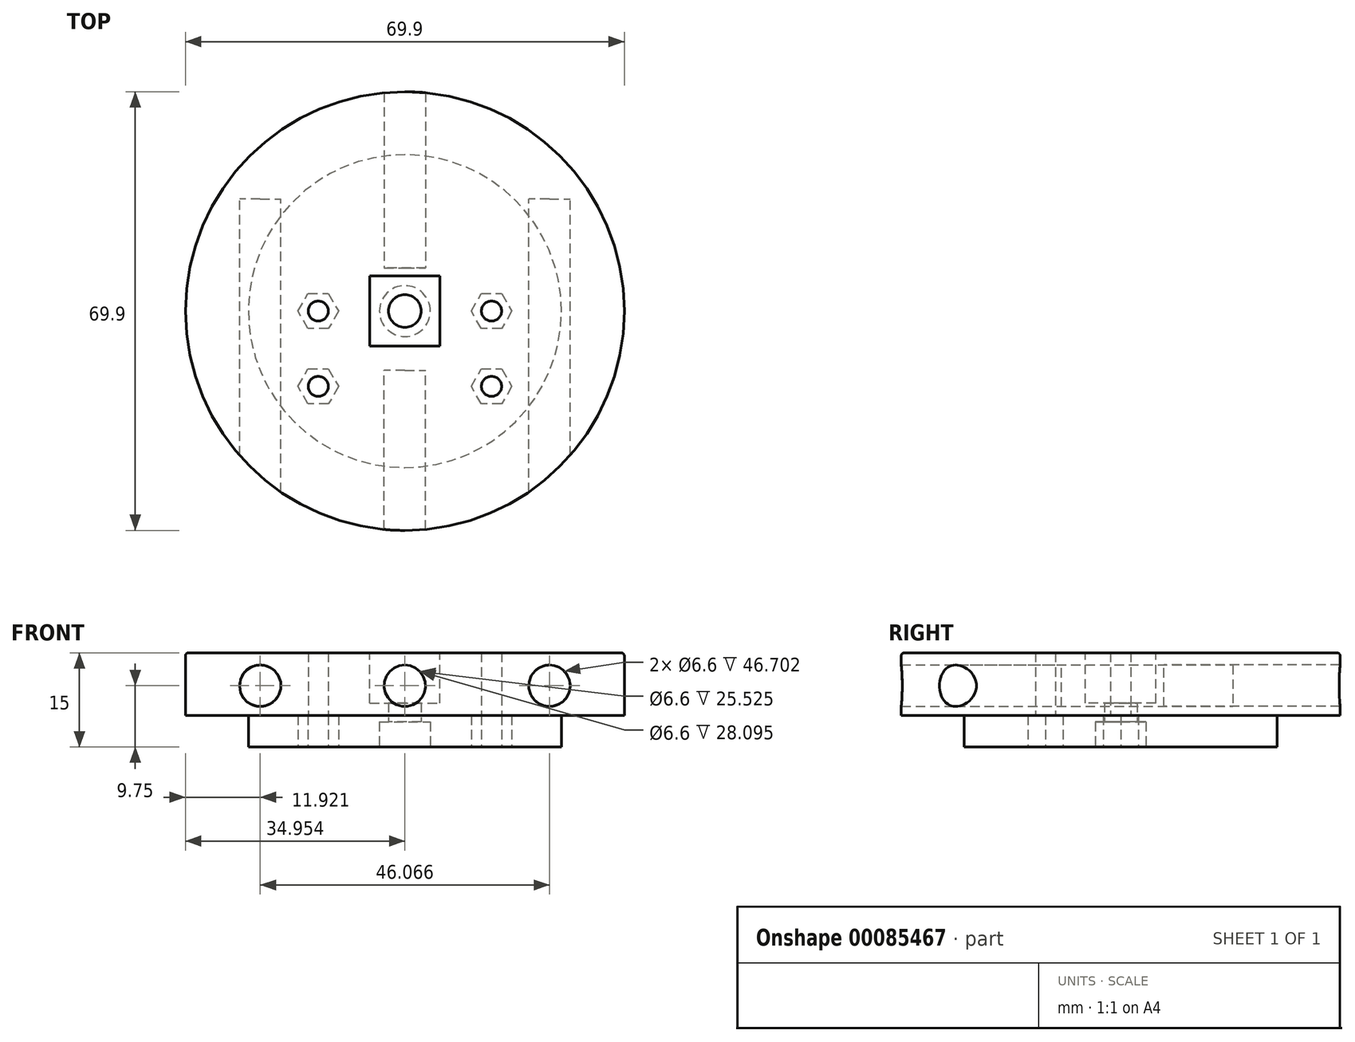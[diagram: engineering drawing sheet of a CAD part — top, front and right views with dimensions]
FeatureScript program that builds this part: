
annotation { "Feature Type Name" : "Feature", "Feature Type Description" : "" }
export const myFeature = defineFeature(function(context is Context, id is Id, definition is map)
    precondition{}
    {
        {
            var Q0;
            Q0=qCreatedBy(makeId("Top.planeOp"),FACE);
            var sketch = newSketch(context, id + "F0", { "sketchPlane" : qUnion([Q0])});
            skCircle(sketch, "E0", {"center": v(30.33, -8.57) * mm, "radius": 34.95 * mm});
            skLineSegment(sketch, "E1.bottom", {"start": v(35.93, -14.17) * mm, "end": v(24.73, -14.17) * mm});
            skLineSegment(sketch, "E1.top", {"start": v(35.93, -2.97) * mm, "end": v(24.73, -2.97) * mm});
            skLineSegment(sketch, "E1.left", {"start": v(35.93, -14.17) * mm, "end": v(35.93, -2.97) * mm});
            skLineSegment(sketch, "E1.right", {"start": v(24.73, -14.17) * mm, "end": v(24.73, -2.97) * mm});
            skPoint(sketch, "E2", {"position": v(24.73, -2.97) * mm});
            skLineSegment(sketch, "E3", {"start": v(30.33, -8.57) * mm, "end": v(5.62, -33.29) * mm, "construction": true});
            skLineSegment(sketch, "E4", {"start": v(30.33, -8.57) * mm, "end": v(55.05, 16.14) * mm, "construction": true});
            skCircle(sketch, "E5", {"center": v(30.33, -8.57) * mm, "radius": 24.93 * mm});
            skLineSegment(sketch, "E6", {"start": v(24.73, -14.17) * mm, "end": v(24.73, -43.07) * mm, "construction": true});
            skLineSegment(sketch, "E7", {"start": v(35.93, -14.17) * mm, "end": v(35.93, -43.07) * mm, "construction": true});
            skPoint(sketch, "E8", {"position": v(16.53, -20.57) * mm});
            skPoint(sketch, "E9", {"position": v(16.53, -8.57) * mm});
            skPoint(sketch, "E10", {"position": v(44.13, -8.57) * mm});
            skPoint(sketch, "E11", {"position": v(44.13, -20.57) * mm});
            skCircle(sketch, "E12.cCircle", {"center": v(16.53, -20.57) * mm, "radius": 3.23 * mm, "construction": true});
            skLineSegment(sketch, "E12.0", {"start": v(19.77, -20.57) * mm, "end": v(18.15, -23.37) * mm});
            skLineSegment(sketch, "E12.1", {"start": v(18.15, -23.37) * mm, "end": v(14.92, -23.37) * mm});
            skLineSegment(sketch, "E12.2", {"start": v(14.92, -23.37) * mm, "end": v(13.3, -20.57) * mm});
            skLineSegment(sketch, "E12.3", {"start": v(13.3, -20.57) * mm, "end": v(14.92, -17.77) * mm});
            skLineSegment(sketch, "E12.4", {"start": v(14.92, -17.77) * mm, "end": v(18.15, -17.77) * mm});
            skLineSegment(sketch, "E12.5", {"start": v(18.15, -17.77) * mm, "end": v(19.77, -20.57) * mm});
            skCircle(sketch, "E13.cCircle", {"center": v(16.53, -8.57) * mm, "radius": 3.23 * mm, "construction": true});
            skLineSegment(sketch, "E13.0", {"start": v(13.3, -8.57) * mm, "end": v(14.92, -5.77) * mm});
            skLineSegment(sketch, "E13.1", {"start": v(14.92, -5.77) * mm, "end": v(18.15, -5.77) * mm});
            skLineSegment(sketch, "E13.2", {"start": v(18.15, -5.77) * mm, "end": v(19.77, -8.57) * mm});
            skLineSegment(sketch, "E13.3", {"start": v(19.77, -8.57) * mm, "end": v(18.15, -11.37) * mm});
            skLineSegment(sketch, "E13.4", {"start": v(18.15, -11.37) * mm, "end": v(14.92, -11.37) * mm});
            skLineSegment(sketch, "E13.5", {"start": v(14.92, -11.37) * mm, "end": v(13.3, -8.57) * mm});
            skCircle(sketch, "E14.cCircle", {"center": v(44.13, -8.57) * mm, "radius": 3.23 * mm, "construction": true});
            skLineSegment(sketch, "E14.0", {"start": v(40.9, -8.57) * mm, "end": v(42.52, -5.77) * mm});
            skLineSegment(sketch, "E14.1", {"start": v(42.52, -5.77) * mm, "end": v(45.75, -5.77) * mm});
            skLineSegment(sketch, "E14.2", {"start": v(45.75, -5.77) * mm, "end": v(47.37, -8.57) * mm});
            skLineSegment(sketch, "E14.3", {"start": v(47.37, -8.57) * mm, "end": v(45.75, -11.37) * mm});
            skLineSegment(sketch, "E14.4", {"start": v(45.75, -11.37) * mm, "end": v(42.52, -11.37) * mm});
            skLineSegment(sketch, "E14.5", {"start": v(42.52, -11.37) * mm, "end": v(40.9, -8.57) * mm});
            skCircle(sketch, "E15.cCircle", {"center": v(44.13, -20.57) * mm, "radius": 3.23 * mm, "construction": true});
            skLineSegment(sketch, "E15.0", {"start": v(47.37, -20.57) * mm, "end": v(45.75, -23.37) * mm});
            skLineSegment(sketch, "E15.1", {"start": v(45.75, -23.37) * mm, "end": v(42.52, -23.37) * mm});
            skLineSegment(sketch, "E15.2", {"start": v(42.52, -23.37) * mm, "end": v(40.9, -20.57) * mm});
            skLineSegment(sketch, "E15.3", {"start": v(40.9, -20.57) * mm, "end": v(42.52, -17.77) * mm});
            skLineSegment(sketch, "E15.4", {"start": v(42.52, -17.77) * mm, "end": v(45.75, -17.77) * mm});
            skLineSegment(sketch, "E15.5", {"start": v(45.75, -17.77) * mm, "end": v(47.37, -20.57) * mm});
            skLineSegment(sketch, "E16", {"start": v(16.53, -8.57) * mm, "end": v(44.13, -8.57) * mm, "construction": true});
            skLineSegment(sketch, "E17", {"start": v(16.53, -20.57) * mm, "end": v(44.13, -20.57) * mm, "construction": true});
            skLineSegment(sketch, "E18", {"start": v(16.53, -8.57) * mm, "end": v(16.53, -20.57) * mm, "construction": true});
            skLineSegment(sketch, "E19", {"start": v(44.13, -20.57) * mm, "end": v(44.13, -8.57) * mm, "construction": true});
            skLineSegment(sketch, "E20", {"start": v(30.33, -20.57) * mm, "end": v(30.33, -8.57) * mm, "construction": true});
            skLineSegment(sketch, "E21", {"start": v(30.33, -8.57) * mm, "end": v(24.73, -8.57) * mm, "construction": true});
            skLineSegment(sketch, "E22", {"start": v(24.73, -8.57) * mm, "end": v(24.73, -20.57) * mm, "construction": true});
            skLineSegment(sketch, "E23", {"start": v(30.33, -8.57) * mm, "end": v(35.93, -8.57) * mm, "construction": true});
            skLineSegment(sketch, "E24", {"start": v(35.93, -8.57) * mm, "end": v(35.93, -20.57) * mm, "construction": true});
            skLineSegment(sketch, "E25", {"start": v(24.73, -8.57) * mm, "end": v(24.73, -14.17) * mm, "construction": true});
            skLineSegment(sketch, "E26", {"start": v(24.73, -8.57) * mm, "end": v(35.93, -8.57) * mm, "construction": true});
            skCircle(sketch, "E27", {"center": v(16.53, -8.57) * mm, "radius": 1.6 * mm});
            skCircle(sketch, "E28", {"center": v(44.13, -8.57) * mm, "radius": 1.6 * mm});
            skCircle(sketch, "E29", {"center": v(44.13, -20.57) * mm, "radius": 1.6 * mm});
            skCircle(sketch, "E30", {"center": v(16.53, -20.57) * mm, "radius": 1.6 * mm});
            skLineSegment(sketch, "E31", {"start": v(30.33, -8.57) * mm, "end": v(-4.62, -8.57) * mm, "construction": true});
            skCircle(sketch, "E32", {"center": v(30.33, -8.57) * mm, "radius": 2.6 * mm});
            skCircle(sketch, "E33", {"center": v(30.33, -8.57) * mm, "radius": 3 * mm});
            skSolve(sketch);
        }
        {
            var Q0;
            Q0=makeQuery(id+"F0.imprint","IMPRINT",FACE,{"disambiguationData":[TD([[makeQuery(id+"F0.imprint","IMPRINT",EDGE,{"derivedFrom":sQuery(id+"F0.wireOp",EDGE,"E0")}),1.0]])]});
            var Q1;
            Q1=makeQuery(id+"F0.imprint","IMPRINT",FACE,{"disambiguationData":[TD([[makeQuery(id+"F0.imprint","IMPRINT",EDGE,{"derivedFrom":sQuery(id+"F0.wireOp",EDGE,"is0V2jlH-Q4Ok-4M3Y-3QFo-iMKSAwjIWmyG.bottom")}),-1.0]])]});
            var Q2;
            Q2=makeQuery(id+"F0.imprint","IMPRINT",FACE,{"disambiguationData":[TD([[makeQuery(id+"F0.imprint","IMPRINT",EDGE,{"derivedFrom":sQuery(id+"F0.wireOp",EDGE,"E1.bottom")}),1.0]])]});
            var Q3;
            {var subQ5=sQuery(id+"F0.wireOp",EDGE,"is0V2jlH-Q4Ok-4M3Y-3QFo-iMKSAwjIWmyG.top");Q3=makeQuery(id+"F0.imprint","IMPRINT",FACE,{"disambiguationData":[TD([[makeQuery(id+"F0.imprint","IMPRINT",EDGE,{"derivedFrom":subQ5}),1.0]])]});}
            var Q4;
            Q4=makeQuery(id+"F0.imprint","IMPRINT",FACE,{"disambiguationData":[TD([[makeQuery(id+"F0.imprint","IMPRINT",EDGE,{"derivedFrom":sQuery(id+"F0.wireOp",EDGE,"E14.0")}),-1.0]])]});
            var Q5;
            {var subQ0=sQuery(id+"F0.wireOp",EDGE,"E15.3");Q5=makeQuery(id+"F0.imprint","IMPRINT",FACE,{"disambiguationData":[TD([[makeQuery(id+"F0.imprint","IMPRINT",EDGE,{"derivedFrom":subQ0}),-1.0]])]});}
            var Q6;
            {var subQ6=sQuery(id+"F0.wireOp",EDGE,"E15.0");Q6=makeQuery(id+"F0.imprint","IMPRINT",FACE,{"disambiguationData":[TD([[makeQuery(id+"F0.imprint","IMPRINT",EDGE,{"derivedFrom":subQ6}),-1.0]])]});}
            var Q7;
            {var subQ0=sQuery(id+"F0.wireOp",EDGE,"E12.4");Q7=makeQuery(id+"F0.imprint","IMPRINT",FACE,{"disambiguationData":[TD([[makeQuery(id+"F0.imprint","IMPRINT",EDGE,{"derivedFrom":subQ0}),-1.0]])]});}
            var Q8;
            {var subQ0=sQuery(id+"F0.wireOp",EDGE,"E12.1");Q8=makeQuery(id+"F0.imprint","IMPRINT",FACE,{"disambiguationData":[TD([[makeQuery(id+"F0.imprint","IMPRINT",EDGE,{"derivedFrom":subQ0}),-1.0]])]});}
            var Q9;
            Q9=makeQuery(id+"F0.imprint","IMPRINT",FACE,{"disambiguationData":[TD([[makeQuery(id+"F0.imprint","IMPRINT",EDGE,{"derivedFrom":sQuery(id+"F0.wireOp",EDGE,"E13.0")}),-1.0]])]});
            var Q10;
            Q10=makeQuery(id+"F0.imprint","IMPRINT",FACE,{"disambiguationData":[TD([[makeQuery(id+"F0.imprint","IMPRINT",EDGE,{"derivedFrom":sQuery(id+"F0.wireOp",EDGE,"E1.bottom")}),-1.0]])]});
            var Q11;
            Q11=makeQuery(id+"F0.imprint","IMPRINT",FACE,{"disambiguationData":[TD([[makeQuery(id+"F0.imprint","IMPRINT",EDGE,{"derivedFrom":sQuery(id+"F0.wireOp",EDGE,"E32")}),-1.0]])]});
            extrude(context, id + "F1", {"entities" : qUnion([Q0, Q1, Q2, Q3, Q4, Q5, Q6, Q7, Q8, Q9, Q10, Q11]), "depth" : 15 * mm});
        }
        {
            var Q0;
            Q0=makeQuery(id+"F1.opExtrude","CAP_EDGE",EDGE,{"disambiguationData":[OSD([sQuery(id+"F0.wireOp",EDGE,"E0")])],"isStart":false});
            fillet(context, id + "F2", {"entities" : qUnion([Q0]), "radius" : .5 * mm, "tangentPropagation" : true, "allowEdgeOverflow" : false});
        }
        {
            var Q0;
            Q0=makeQuery(id+"F0.imprint","IMPRINT",FACE,{"disambiguationData":[TD([[makeQuery(id+"F0.imprint","IMPRINT",EDGE,{"derivedFrom":sQuery(id+"F0.wireOp",EDGE,"E0")}),1.0]])]});
            extrude(context, id + "F3", {"entities" : qUnion([Q0]), "operationType" : NewBodyOperationType.REMOVE, "depth" : 4.75 * mm});
        }
        {
            var Q0;
            {var subQ0=sQuery(id+"F0.wireOp",EDGE,"E1.right");var subQ1=sQuery(id+"F0.wireOp",EDGE,"E1.left");var subQ2=sQuery(id+"F0.wireOp",EDGE,"E1.top");var subQ3=sQuery(id+"F0.wireOp",EDGE,"E1.bottom");Q0=makeQuery(id+"FWqoJOTwQ8Ntj7Z_0.boolean.opBoolean","MERGE",FACE,{"derivedFrom":[makeQuery(id+"F1.opExtrude","CAP_FACE",FACE,{"disambiguationData":[OSD([sQuery(id+"F0.wireOp",EDGE,"E0"),subQ3,subQ2,subQ1,subQ0])],"isStart":true}),makeQuery(id+"FWqoJOTwQ8Ntj7Z_0.opExtrude","CAP_FACE",FACE,{"disambiguationData":[OSD([subQ3,subQ2,subQ1,subQ0])],"isStart":true})]});}
            var sketch = newSketch(context, id + "F4", { "sketchPlane" : qUnion([Q0])});
            skLineSegment(sketch, "E34", {"start": v(30.33, 33.5) * mm, "end": v(30.33, -16.35) * mm, "construction": true});
            skCircle(sketch, "E35", {"center": v(30.33, 8.57) * mm, "radius": 4.05 * mm});
            skCircle(sketch, "E36", {"center": v(30.33, 8.57) * mm, "radius": 1.6 * mm});
            skSolve(sketch);
        }
        {
            var Q0;
            Q0=makeQuery(id+"F4.imprint","IMPRINT",FACE,{"disambiguationData":[TD([[makeQuery(id+"F4.imprint","IMPRINT",EDGE,{"derivedFrom":sQuery(id+"F4.wireOp",EDGE,"E35")}),1.0]])]});
            var Q1;
            Q1=makeQuery(id+"F0.imprint","IMPRINT",FACE,{"disambiguationData":[TD([[makeQuery(id+"F0.imprint","IMPRINT",EDGE,{"derivedFrom":sQuery(id+"F0.wireOp",EDGE,"E32")}),-1.0]])]});
            extrude(context, id + "F5", {"entities" : qUnion([Q0, Q1]), "operationType" : NewBodyOperationType.REMOVE, "oppositeDirection" : true, "depth" : 4 * mm});
        }
        {
            var Q0;
            {var subQ0=sQuery(id+"F0.wireOp",EDGE,"E15.2");Q0=makeQuery(id+"F0.imprint","IMPRINT",FACE,{"disambiguationData":[TD([[makeQuery(id+"F0.imprint","IMPRINT",EDGE,{"derivedFrom":subQ0}),-1.0]])]});}
            var Q1;
            {var subQ0=sQuery(id+"F0.wireOp",EDGE,"E15.1");var subQ1=sQuery(id+"F0.wireOp",EDGE,"E5");var subQ2=makeQuery(id+"F0.imprint","INTERSECT",VERTEX,{"derivedFrom":[subQ1,subQ0]});Q1=makeQuery(id+"F0.imprint","IMPRINT",FACE,{"disambiguationData":[TD([[makeQuery(id+"F0.imprint","IMPRINT",EDGE,{"disambiguationData":[TD([[subQ2,-1.0]])],"derivedFrom":subQ1}),-1.0]])]});}
            var Q2;
            Q2=makeQuery(id+"F0.imprint","IMPRINT",FACE,{"disambiguationData":[TD([[makeQuery(id+"F0.imprint","IMPRINT",EDGE,{"derivedFrom":sQuery(id+"F0.wireOp",EDGE,"E14.0")}),-1.0]])]});
            var Q3;
            Q3=makeQuery(id+"F0.imprint","IMPRINT",FACE,{"disambiguationData":[TD([[makeQuery(id+"F0.imprint","IMPRINT",EDGE,{"derivedFrom":sQuery(id+"F0.wireOp",EDGE,"E13.0")}),-1.0]])]});
            var Q4;
            {var subQ0=sQuery(id+"F0.wireOp",EDGE,"E12.1");var subQ1=sQuery(id+"F0.wireOp",EDGE,"E5");var subQ2=makeQuery(id+"F0.imprint","INTERSECT",VERTEX,{"derivedFrom":[subQ1,subQ0]});Q4=makeQuery(id+"F0.imprint","IMPRINT",FACE,{"disambiguationData":[TD([[makeQuery(id+"F0.imprint","IMPRINT",EDGE,{"disambiguationData":[TD([[subQ2,1.0]])],"derivedFrom":subQ1}),-1.0]])]});}
            var Q5;
            {var subQ5=sQuery(id+"F0.wireOp",EDGE,"E12.0");Q5=makeQuery(id+"F0.imprint","IMPRINT",FACE,{"disambiguationData":[TD([[makeQuery(id+"F0.imprint","IMPRINT",EDGE,{"derivedFrom":subQ5}),-1.0]])]});}
            extrude(context, id + "F6", {"entities" : qUnion([Q0, Q1, Q2, Q3, Q4, Q5]), "operationType" : NewBodyOperationType.REMOVE, "depth" : 5 * mm});
        }
        {
            var Q0;
            Q0=makeQuery(id+"F1.opExtrude","CAP_FACE",FACE,{"disambiguationData":[OSD([sQuery(id+"F0.wireOp",EDGE,"E0"),sQuery(id+"F0.wireOp",EDGE,"E27"),sQuery(id+"F0.wireOp",EDGE,"E28"),sQuery(id+"F0.wireOp",EDGE,"E29"),sQuery(id+"F0.wireOp",EDGE,"E30")])],"isStart":false});
            var sketch = newSketch(context, id + "F7", { "sketchPlane" : qUnion([Q0])});
            skLineSegment(sketch, "E37.bottom", {"start": v(24.73, -2.97) * mm, "end": v(35.93, -2.97) * mm});
            skLineSegment(sketch, "E37.top", {"start": v(24.73, -14.17) * mm, "end": v(35.93, -14.17) * mm});
            skLineSegment(sketch, "E37.left", {"start": v(24.73, -2.97) * mm, "end": v(24.73, -14.17) * mm});
            skLineSegment(sketch, "E37.right", {"start": v(35.93, -2.97) * mm, "end": v(35.93, -14.17) * mm});
            skPoint(sketch, "E37.middle", {"position": v(30.33, -8.57) * mm});
            skSolve(sketch);
        }
        {
            var Q0;
            Q0=makeQuery(id+"F7.imprint","IMPRINT",FACE,{"disambiguationData":[TD([[makeQuery(id+"F7.imprint","IMPRINT",EDGE,{"derivedFrom":sQuery(id+"F7.wireOp",EDGE,"E37.bottom")}),-1.0]])]});
            var Q1;
            Q1=makeQuery(id+"F7.imprint","IMPRINT",FACE,{"disambiguationData":[TD([[makeQuery(id+"F7.imprint","IMPRINT",EDGE,{"derivedFrom":sQuery(id+"F7.wireOp",EDGE,"KLjTeYKa-iTZI-HRHy-V6Gp-klRxXlumgHrG")}),1.0]])]});
            extrude(context, id + "F8", {"entities" : qUnion([Q0, Q1]), "operationType" : NewBodyOperationType.REMOVE, "oppositeDirection" : true, "depth" : 8 * mm});
        }
        {
            var Q0;
            Q0=makeQuery(id+"F0.imprint","IMPRINT",FACE,{"disambiguationData":[TD([[makeQuery(id+"F0.imprint","IMPRINT",EDGE,{"derivedFrom":sQuery(id+"F0.wireOp",EDGE,"E32")}),1.0]])]});
            extrude(context, id + "F9", {"entities" : qUnion([Q0]), "operationType" : NewBodyOperationType.REMOVE, "oppositeDirection" : true, "depth" : 35.94 * mm});
        }
        {
            var Q0;
            Q0=qCreatedBy(makeId("Front.planeOp"),FACE);
            var sketch = newSketch(context, id + "F10", { "sketchPlane" : qUnion([Q0])});
            skLineSegment(sketch, "E38", {"start": v(16.53, 0) * mm, "end": v(16.53, 14.5) * mm});
            skLineSegment(sketch, "E39", {"start": v(44.13, 0) * mm, "end": v(44.13, 14.5) * mm});
            skLineSegment(sketch, "E40", {"start": v(24.73, 0) * mm, "end": v(24.73, 14.5) * mm});
            skLineSegment(sketch, "E41", {"start": v(35.93, 0) * mm, "end": v(35.93, 14.5) * mm});
            skLineSegment(sketch, "E42", {"start": v(19.77, 0) * mm, "end": v(19.77, 14.5) * mm});
            skLineSegment(sketch, "E43", {"start": v(40.9, 0) * mm, "end": v(40.9, 14.5) * mm});
            skPoint(sketch, "E44", {"position": v(30.33, 5) * mm});
            skPoint(sketch, "E45", {"position": v(30.33, 14.5) * mm});
            skCircle(sketch, "E46", {"center": v(30.33, 9.75) * mm, "radius": 3.3 * mm});
            skLineSegment(sketch, "E47.trimOffspring", {"start": v(30.33, 13.05) * mm, "end": v(30.33, 14.5) * mm});
            skPoint(sketch, "E48", {"position": v(47.37, 5) * mm});
            skPoint(sketch, "E49", {"position": v(13.3, 5) * mm});
            skPoint(sketch, "E50", {"position": v(13.3, 14.5) * mm});
            skPoint(sketch, "E51", {"position": v(47.37, 14.5) * mm});
            skLineSegment(sketch, "E52", {"start": v(13.3, 5) * mm, "end": v(13.3, 14.5) * mm});
            skLineSegment(sketch, "E53", {"start": v(47.37, 14.5) * mm, "end": v(47.37, 5) * mm});
            skLineSegment(sketch, "E54", {"start": v(47.37, 9.75) * mm, "end": v(53.37, 9.75) * mm});
            skLineSegment(sketch, "E55", {"start": v(13.3, 9.75) * mm, "end": v(7.3, 9.75) * mm});
            skCircle(sketch, "E56", {"center": v(7.3, 9.75) * mm, "radius": 3.3 * mm});
            skCircle(sketch, "E57", {"center": v(53.37, 9.75) * mm, "radius": 3.3 * mm});
            skSolve(sketch);
        }
        {
            var Q0;
            Q0 = qSketchRegion(id + "F10", true);
            extrude(context, id + "F11", {"entities" : qUnion([Q0]), "operationType" : NewBodyOperationType.REMOVE, "depth" : 54.69 * mm, "hasSecondDirection" : true, "secondDirectionOppositeDirection" : false, "secondDirectionDepth" : 18 * mm});
        }
        {
            var Q0;
            Q0=makeQuery(id+"F11.boolean.opBoolean","COPY",FACE,{"derivedFrom":makeQuery(id+"F11.opExtrude","CAP_FACE",FACE,{"disambiguationData":[OSD([sQuery(id+"F10.wireOp",EDGE,"E46")])],"isStart":true})});
            extrude(context, id + "F12", {"entities" : qUnion([Q0]), "operationType" : NewBodyOperationType.REMOVE, "oppositeDirection" : true, "depth" : 47.5 * mm, "hasSecondDirection" : true, "secondDirectionOppositeDirection" : true, "secondDirectionDepth" : 16.28 * mm});
        }
        {
            var Q0;
            Q0=makeQuery(id+"F11.boolean.opBoolean","COPY",FACE,{"derivedFrom":makeQuery(id+"F11.opExtrude","CAP_FACE",FACE,{"disambiguationData":[OSD([sQuery(id+"F10.wireOp",EDGE,"E56")])],"isStart":true})});
            var Q1;
            Q1=makeQuery(id+"F11.boolean.opBoolean","COPY",FACE,{"derivedFrom":makeQuery(id+"F11.opExtrude","CAP_FACE",FACE,{"disambiguationData":[OSD([sQuery(id+"F10.wireOp",EDGE,"E57")])],"isStart":true})});
            extrude(context, id + "F13", {"entities" : qUnion([Q0, Q1]), "operationType" : NewBodyOperationType.REMOVE, "oppositeDirection" : true, "depth" : 27.28 * mm});
        }
    });
